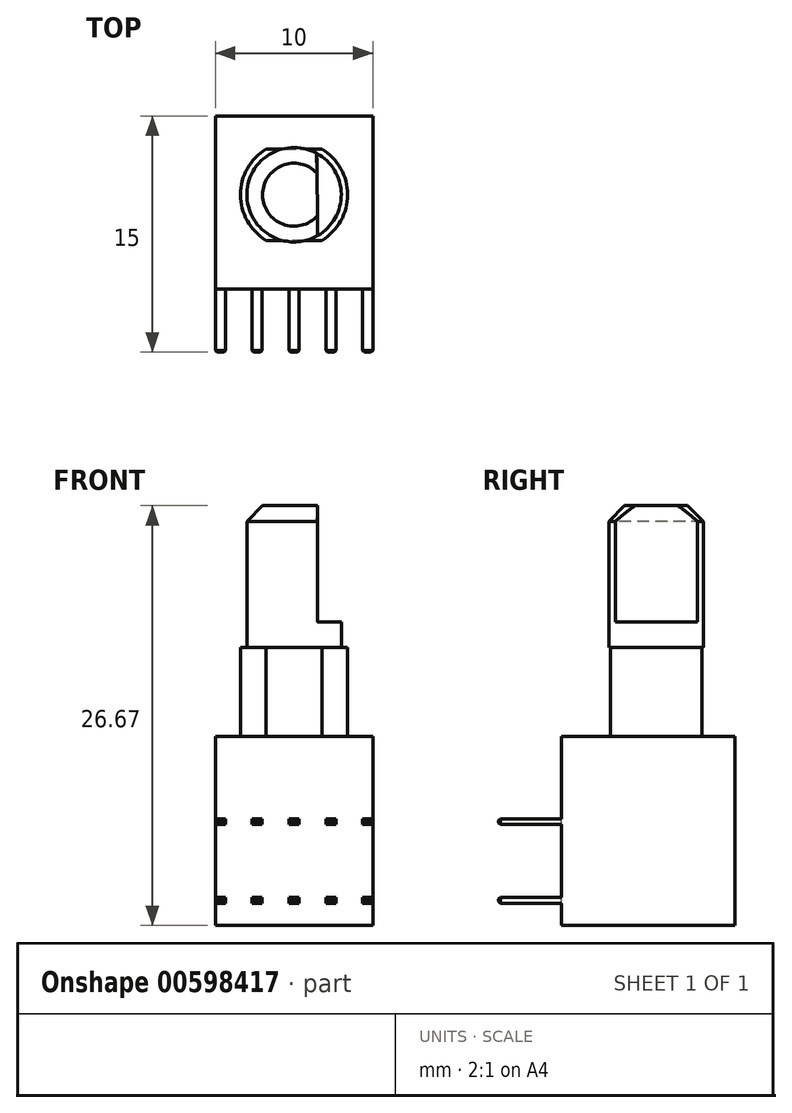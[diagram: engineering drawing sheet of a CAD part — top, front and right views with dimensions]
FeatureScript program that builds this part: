
annotation { "Feature Type Name" : "Feature", "Feature Type Description" : "" }
export const myFeature = defineFeature(function(context is Context, id is Id, definition is map)
    precondition{}
    {
        {
            var Q0;
            Q0=qCreatedBy(makeId("Top.planeOp"),FACE);
            var sketch = newSketch(context, id + "F0", { "sketchPlane" : qUnion([Q0])});
            skLineSegment(sketch, "E0.bottom", {"start": v(5, 5.5) * mm, "end": v(-5, 5.5) * mm});
            skLineSegment(sketch, "E0.top", {"start": v(5, -5.5) * mm, "end": v(-5, -5.5) * mm});
            skLineSegment(sketch, "E0.left", {"start": v(5, 5.5) * mm, "end": v(5, -5.5) * mm});
            skLineSegment(sketch, "E0.right", {"start": v(-5, 5.5) * mm, "end": v(-5, -5.5) * mm});
            skPoint(sketch, "E0.middle", {"position": v(0, 0) * mm});
            skSolve(sketch);
        }
        {
            var Q0;
            Q0=qSketchRegion(id+"F0",true);
            var Q1;
            Q1=makeQuery(id+"F0.imprint","IMPRINT",FACE,{"disambiguationData":[TD([[makeQuery(id+"F0.imprint","IMPRINT",EDGE,{"derivedFrom":sQuery(id+"F0.wireOp",EDGE,"E0.bottom")}),1.0]])]});
            extrude(context, id + "F1", {"entities" : qUnion([Q0, Q1]), "depth" : 12 * mm, "offsetDistance" : 25 * mm});
        }
        {
            var Q0;
            Q0=makeQuery(id+"F1.opExtrude","CAP_FACE",FACE,{"disambiguationData":[OSD([sQuery(id+"F0.wireOp",EDGE,"E0.bottom"),sQuery(id+"F0.wireOp",EDGE,"E0.top"),sQuery(id+"F0.wireOp",EDGE,"E0.left"),sQuery(id+"F0.wireOp",EDGE,"E0.right")])],"isStart":false});
            var sketch = newSketch(context, id + "F2", { "sketchPlane" : qUnion([Q0])});
            skLineSegment(sketch, "E1", {"start": v(-5, 3.4) * mm, "end": v(5, 3.4) * mm, "construction": true});
            skLineSegment(sketch, "E2", {"start": v(-5, -2.4) * mm, "end": v(5, -2.4) * mm, "construction": true});
            skCircle(sketch, "E3", {"center": v(0, 0.5) * mm, "radius": 3.4 * mm});
            skLineSegment(sketch, "E4", {"start": v(-1.77, 3.4) * mm, "end": v(1.77, 3.4) * mm});
            skLineSegment(sketch, "E5", {"start": v(1.77, -2.4) * mm, "end": v(-1.77, -2.4) * mm});
            skSolve(sketch);
        }
        {
            var Q0;
            {var subQ0=sQuery(id+"F2.wireOp",EDGE,"E4");Q0=makeQuery(id+"F2.imprint","IMPRINT",FACE,{"disambiguationData":[TD([[makeQuery(id+"F2.imprint","IMPRINT",EDGE,{"derivedFrom":subQ0}),-1.0]])]});}
            extrude(context, id + "F3", {"entities" : qUnion([Q0]), "operationType" : NewBodyOperationType.ADD, "depth" : 5.67 * mm, "offsetDistance" : 25 * mm});
        }
        {
            var Q0;
            Q0=makeQuery(id+"F3.opExtrude","CAP_FACE",FACE,{"disambiguationData":[OSD([sQuery(id+"F2.wireOp",EDGE,"E3"),sQuery(id+"F2.wireOp",EDGE,"E4"),sQuery(id+"F2.wireOp",EDGE,"E5")])],"isStart":false});
            var sketch = newSketch(context, id + "F4", { "sketchPlane" : qUnion([Q0])});
            skCircle(sketch, "E6", {"center": v(0, 0.5) * mm, "radius": 3 * mm});
            skLineSegment(sketch, "E7", {"start": v(1.44, 3.13) * mm, "end": v(1.5, -2.1) * mm});
            skSolve(sketch);
        }
        {
            var Q0;
            {var subQ0=sQuery(id+"F4.wireOp",EDGE,"E7");Q0=makeQuery(id+"F4.imprint","IMPRINT",FACE,{"disambiguationData":[TD([[makeQuery(id+"F4.imprint","IMPRINT",EDGE,{"derivedFrom":subQ0}),1.0]])]});}
            extrude(context, id + "F5", {"entities" : qUnion([Q0]), "operationType" : NewBodyOperationType.ADD, "depth" : 1.6 * mm, "offsetDistance" : 25 * mm});
        }
        {
            var Q0;
            {var subQ0=sQuery(id+"F4.wireOp",EDGE,"E7");Q0=makeQuery(id+"F4.imprint","IMPRINT",FACE,{"disambiguationData":[TD([[makeQuery(id+"F4.imprint","IMPRINT",EDGE,{"derivedFrom":subQ0}),-1.0]])]});}
            var Q1;
            {var subQ0=sQuery(id+"F4.wireOp",EDGE,"E6");var subQ1=makeQuery(id+"F3.opExtrude","CAP_EDGE",EDGE,{"disambiguationData":[OSD([sQuery(id+"F2.wireOp",EDGE,"E5")])],"isStart":false});var subQ2=makeQuery(id+"F4.imprint","INTERSECT",VERTEX,{"disambiguationData":[OD(0.0)],"derivedFrom":[subQ1,subQ0]});Q1=makeQuery(id+"F4.imprint","IMPRINT",FACE,{"disambiguationData":[TD([[makeQuery(id+"F4.imprint","IMPRINT",EDGE,{"disambiguationData":[TD([[subQ2,-1.0]])],"derivedFrom":subQ0}),1.0]])]});}
            var Q2;
            {var subQ0=sQuery(id+"F4.wireOp",EDGE,"E6");var subQ1=makeQuery(id+"F3.opExtrude","CAP_EDGE",EDGE,{"disambiguationData":[OSD([sQuery(id+"F2.wireOp",EDGE,"E4")])],"isStart":false});var subQ2=makeQuery(id+"F4.imprint","INTERSECT",VERTEX,{"disambiguationData":[OD(0.0)],"derivedFrom":[subQ1,subQ0]});Q2=makeQuery(id+"F4.imprint","IMPRINT",FACE,{"disambiguationData":[TD([[makeQuery(id+"F4.imprint","IMPRINT",EDGE,{"disambiguationData":[TD([[subQ2,-1.0]])],"derivedFrom":subQ0}),1.0]])]});}
            extrude(context, id + "F6", {"entities" : qUnion([Q0, Q1, Q2]), "operationType" : NewBodyOperationType.ADD, "depth" : 9 * mm, "offsetDistance" : 25 * mm});
        }
        {
            var Q0;
            Q0=makeQuery(id+"F6.opExtrude","CAP_EDGE",EDGE,{"disambiguationData":[OSD([sQuery(id+"F4.wireOp",EDGE,"E6")])],"isStart":false});
            chamfer(context, id + "F7", {"entities" : qUnion([Q0]), "width" : 1 * mm, "tangentPropagation" : true});
        }
        {
            var Q0;
            Q0=makeQuery(id+"F1.opExtrude","SWEPT_FACE",FACE,{"disambiguationData":[OSD([sQuery(id+"F0.wireOp",EDGE,"E0.top")])]});
            var sketch = newSketch(context, id + "F8", { "sketchPlane" : qUnion([Q0])});
            skLineSegment(sketch, "E8.bottom", {"start": v(-5, 1.42) * mm, "end": v(-4.36, 1.42) * mm});
            skLineSegment(sketch, "E8.top", {"start": v(-5, 1.78) * mm, "end": v(-4.36, 1.78) * mm});
            skLineSegment(sketch, "E8.left", {"start": v(-5, 1.42) * mm, "end": v(-5, 1.78) * mm});
            skLineSegment(sketch, "E8.right", {"start": v(-4.36, 1.42) * mm, "end": v(-4.36, 1.78) * mm});
            skLineSegment(sketch, "E9.0.1.0", {"start": v(-5, 6.42) * mm, "end": v(-4.36, 6.42) * mm});
            skLineSegment(sketch, "E9.0.1.1", {"start": v(-5, 6.42) * mm, "end": v(-5, 6.78) * mm});
            skLineSegment(sketch, "E9.0.1.2", {"start": v(-4.36, 6.42) * mm, "end": v(-4.36, 6.78) * mm});
            skLineSegment(sketch, "E9.0.1.3", {"start": v(-5, 6.78) * mm, "end": v(-4.36, 6.78) * mm});
            skLineSegment(sketch, "E9.1.0.0", {"start": v(-2.66, 1.42) * mm, "end": v(-2.02, 1.42) * mm});
            skLineSegment(sketch, "E9.1.0.1", {"start": v(-2.66, 1.42) * mm, "end": v(-2.66, 1.78) * mm});
            skLineSegment(sketch, "E9.1.0.2", {"start": v(-2.02, 1.42) * mm, "end": v(-2.02, 1.78) * mm});
            skLineSegment(sketch, "E9.1.0.3", {"start": v(-2.66, 1.78) * mm, "end": v(-2.02, 1.78) * mm});
            skLineSegment(sketch, "E9.1.1.0", {"start": v(-2.66, 6.42) * mm, "end": v(-2.02, 6.42) * mm});
            skLineSegment(sketch, "E9.1.1.1", {"start": v(-2.66, 6.42) * mm, "end": v(-2.66, 6.78) * mm});
            skLineSegment(sketch, "E9.1.1.2", {"start": v(-2.02, 6.42) * mm, "end": v(-2.02, 6.78) * mm});
            skLineSegment(sketch, "E9.1.1.3", {"start": v(-2.66, 6.78) * mm, "end": v(-2.02, 6.78) * mm});
            skLineSegment(sketch, "E9.2.0.0", {"start": v(-0.32, 1.42) * mm, "end": v(0.32, 1.42) * mm});
            skLineSegment(sketch, "E9.2.0.1", {"start": v(-0.32, 1.42) * mm, "end": v(-0.32, 1.78) * mm});
            skLineSegment(sketch, "E9.2.0.2", {"start": v(0.32, 1.42) * mm, "end": v(0.32, 1.78) * mm});
            skLineSegment(sketch, "E9.2.0.3", {"start": v(-0.32, 1.78) * mm, "end": v(0.32, 1.78) * mm});
            skLineSegment(sketch, "E9.2.1.0", {"start": v(-0.32, 6.42) * mm, "end": v(0.32, 6.42) * mm});
            skLineSegment(sketch, "E9.2.1.1", {"start": v(-0.32, 6.42) * mm, "end": v(-0.32, 6.78) * mm});
            skLineSegment(sketch, "E9.2.1.2", {"start": v(0.32, 6.42) * mm, "end": v(0.32, 6.78) * mm});
            skLineSegment(sketch, "E9.2.1.3", {"start": v(-0.32, 6.78) * mm, "end": v(0.32, 6.78) * mm});
            skLineSegment(sketch, "E9.3.0.0", {"start": v(2.02, 1.42) * mm, "end": v(2.66, 1.42) * mm});
            skLineSegment(sketch, "E9.3.0.1", {"start": v(2.02, 1.42) * mm, "end": v(2.02, 1.78) * mm});
            skLineSegment(sketch, "E9.3.0.2", {"start": v(2.66, 1.42) * mm, "end": v(2.66, 1.78) * mm});
            skLineSegment(sketch, "E9.3.0.3", {"start": v(2.02, 1.78) * mm, "end": v(2.66, 1.78) * mm});
            skLineSegment(sketch, "E9.3.1.0", {"start": v(2.02, 6.42) * mm, "end": v(2.66, 6.42) * mm});
            skLineSegment(sketch, "E9.3.1.1", {"start": v(2.02, 6.42) * mm, "end": v(2.02, 6.78) * mm});
            skLineSegment(sketch, "E9.3.1.2", {"start": v(2.66, 6.42) * mm, "end": v(2.66, 6.78) * mm});
            skLineSegment(sketch, "E9.3.1.3", {"start": v(2.02, 6.78) * mm, "end": v(2.66, 6.78) * mm});
            skLineSegment(sketch, "E9.4.0.0", {"start": v(4.36, 1.42) * mm, "end": v(5, 1.42) * mm});
            skLineSegment(sketch, "E9.4.0.1", {"start": v(4.36, 1.42) * mm, "end": v(4.36, 1.78) * mm});
            skLineSegment(sketch, "E9.4.0.2", {"start": v(5, 1.42) * mm, "end": v(5, 1.78) * mm});
            skLineSegment(sketch, "E9.4.0.3", {"start": v(4.36, 1.78) * mm, "end": v(5, 1.78) * mm});
            skLineSegment(sketch, "E9.4.1.0", {"start": v(4.36, 6.42) * mm, "end": v(5, 6.42) * mm});
            skLineSegment(sketch, "E9.4.1.1", {"start": v(4.36, 6.42) * mm, "end": v(4.36, 6.78) * mm});
            skLineSegment(sketch, "E9.4.1.2", {"start": v(5, 6.42) * mm, "end": v(5, 6.78) * mm});
            skLineSegment(sketch, "E9.4.1.3", {"start": v(4.36, 6.78) * mm, "end": v(5, 6.78) * mm});
            skLineSegment(sketch, "E9.direction1", {"start": v(-5, 1.42) * mm, "end": v(-2.66, 1.42) * mm, "construction": true});
            skLineSegment(sketch, "E9.direction2", {"start": v(-5, 1.42) * mm, "end": v(-5, 6.42) * mm, "construction": true});
            skSolve(sketch);
        }
        {
            var Q0;
            Q0=makeQuery(id+"F8.imprint","IMPRINT",FACE,{"disambiguationData":[TD([[makeQuery(id+"F8.imprint","IMPRINT",EDGE,{"derivedFrom":sQuery(id+"F8.wireOp",EDGE,"E9.0.1.0")}),1.0]])]});
            var Q1;
            Q1=makeQuery(id+"F8.imprint","IMPRINT",FACE,{"disambiguationData":[TD([[makeQuery(id+"F8.imprint","IMPRINT",EDGE,{"derivedFrom":sQuery(id+"F8.wireOp",EDGE,"E9.1.1.0")}),1.0]])]});
            var Q2;
            Q2=makeQuery(id+"F8.imprint","IMPRINT",FACE,{"disambiguationData":[TD([[makeQuery(id+"F8.imprint","IMPRINT",EDGE,{"derivedFrom":sQuery(id+"F8.wireOp",EDGE,"E9.2.1.0")}),1.0]])]});
            var Q3;
            Q3=makeQuery(id+"F8.imprint","IMPRINT",FACE,{"disambiguationData":[TD([[makeQuery(id+"F8.imprint","IMPRINT",EDGE,{"derivedFrom":sQuery(id+"F8.wireOp",EDGE,"E9.4.0.0")}),1.0]])]});
            var Q4;
            Q4=makeQuery(id+"F8.imprint","IMPRINT",FACE,{"disambiguationData":[TD([[makeQuery(id+"F8.imprint","IMPRINT",EDGE,{"derivedFrom":sQuery(id+"F8.wireOp",EDGE,"E9.3.0.0")}),1.0]])]});
            var Q5;
            Q5=makeQuery(id+"F8.imprint","IMPRINT",FACE,{"disambiguationData":[TD([[makeQuery(id+"F8.imprint","IMPRINT",EDGE,{"derivedFrom":sQuery(id+"F8.wireOp",EDGE,"E9.2.0.0")}),1.0]])]});
            var Q6;
            Q6=makeQuery(id+"F8.imprint","IMPRINT",FACE,{"disambiguationData":[TD([[makeQuery(id+"F8.imprint","IMPRINT",EDGE,{"derivedFrom":sQuery(id+"F8.wireOp",EDGE,"E9.1.0.0")}),1.0]])]});
            var Q7;
            Q7=makeQuery(id+"F8.imprint","IMPRINT",FACE,{"disambiguationData":[TD([[makeQuery(id+"F8.imprint","IMPRINT",EDGE,{"derivedFrom":sQuery(id+"F8.wireOp",EDGE,"E8.bottom")}),1.0]])]});
            var Q8;
            Q8=makeQuery(id+"F8.imprint","IMPRINT",FACE,{"disambiguationData":[TD([[makeQuery(id+"F8.imprint","IMPRINT",EDGE,{"derivedFrom":sQuery(id+"F8.wireOp",EDGE,"E9.3.1.0")}),1.0]])]});
            var Q9;
            Q9=makeQuery(id+"F8.imprint","IMPRINT",FACE,{"disambiguationData":[TD([[makeQuery(id+"F8.imprint","IMPRINT",EDGE,{"derivedFrom":sQuery(id+"F8.wireOp",EDGE,"E9.4.1.0")}),1.0]])]});
            extrude(context, id + "F9", {"entities" : qUnion([Q0, Q1, Q2, Q3, Q4, Q5, Q6, Q7, Q8, Q9]), "operationType" : NewBodyOperationType.ADD, "depth" : 4 * mm, "offsetDistance" : 25 * mm});
        }
        {
            var Q0;
            Q0=makeQuery(id+"F9.opExtrude","CAP_FACE",FACE,{"disambiguationData":[OSD([sQuery(id+"F8.wireOp",EDGE,"E9.0.1.0"),sQuery(id+"F8.wireOp",EDGE,"E9.0.1.1"),sQuery(id+"F8.wireOp",EDGE,"E9.0.1.2"),sQuery(id+"F8.wireOp",EDGE,"E9.0.1.3")])],"isStart":false});
            var Q1;
            Q1=makeQuery(id+"F9.opExtrude","CAP_FACE",FACE,{"disambiguationData":[OSD([sQuery(id+"F8.wireOp",EDGE,"E9.1.1.0"),sQuery(id+"F8.wireOp",EDGE,"E9.1.1.1"),sQuery(id+"F8.wireOp",EDGE,"E9.1.1.2"),sQuery(id+"F8.wireOp",EDGE,"E9.1.1.3")])],"isStart":false});
            var Q2;
            Q2=makeQuery(id+"F9.opExtrude","CAP_FACE",FACE,{"disambiguationData":[OSD([sQuery(id+"F8.wireOp",EDGE,"E9.2.1.0"),sQuery(id+"F8.wireOp",EDGE,"E9.2.1.1"),sQuery(id+"F8.wireOp",EDGE,"E9.2.1.2"),sQuery(id+"F8.wireOp",EDGE,"E9.2.1.3")])],"isStart":false});
            var Q3;
            Q3=makeQuery(id+"F9.opExtrude","CAP_FACE",FACE,{"disambiguationData":[OSD([sQuery(id+"F8.wireOp",EDGE,"E9.3.1.0"),sQuery(id+"F8.wireOp",EDGE,"E9.3.1.1"),sQuery(id+"F8.wireOp",EDGE,"E9.3.1.2"),sQuery(id+"F8.wireOp",EDGE,"E9.3.1.3")])],"isStart":false});
            var Q4;
            Q4=makeQuery(id+"F9.opExtrude","CAP_FACE",FACE,{"disambiguationData":[OSD([sQuery(id+"F8.wireOp",EDGE,"E9.4.1.0"),sQuery(id+"F8.wireOp",EDGE,"E9.4.1.1"),sQuery(id+"F8.wireOp",EDGE,"E9.4.1.2"),sQuery(id+"F8.wireOp",EDGE,"E9.4.1.3")])],"isStart":false});
            var Q5;
            Q5=makeQuery(id+"F9.opExtrude","CAP_FACE",FACE,{"disambiguationData":[OSD([sQuery(id+"F8.wireOp",EDGE,"E9.4.0.0"),sQuery(id+"F8.wireOp",EDGE,"E9.4.0.1"),sQuery(id+"F8.wireOp",EDGE,"E9.4.0.2"),sQuery(id+"F8.wireOp",EDGE,"E9.4.0.3")])],"isStart":false});
            var Q6;
            Q6=makeQuery(id+"F9.opExtrude","CAP_FACE",FACE,{"disambiguationData":[OSD([sQuery(id+"F8.wireOp",EDGE,"E9.3.0.0"),sQuery(id+"F8.wireOp",EDGE,"E9.3.0.1"),sQuery(id+"F8.wireOp",EDGE,"E9.3.0.2"),sQuery(id+"F8.wireOp",EDGE,"E9.3.0.3")])],"isStart":false});
            var Q7;
            Q7=makeQuery(id+"F9.opExtrude","CAP_FACE",FACE,{"disambiguationData":[OSD([sQuery(id+"F8.wireOp",EDGE,"E9.2.0.0"),sQuery(id+"F8.wireOp",EDGE,"E9.2.0.1"),sQuery(id+"F8.wireOp",EDGE,"E9.2.0.2"),sQuery(id+"F8.wireOp",EDGE,"E9.2.0.3")])],"isStart":false});
            var Q8;
            Q8=makeQuery(id+"F9.opExtrude","CAP_FACE",FACE,{"disambiguationData":[OSD([sQuery(id+"F8.wireOp",EDGE,"E9.1.0.0"),sQuery(id+"F8.wireOp",EDGE,"E9.1.0.1"),sQuery(id+"F8.wireOp",EDGE,"E9.1.0.2"),sQuery(id+"F8.wireOp",EDGE,"E9.1.0.3")])],"isStart":false});
            var Q9;
            Q9=makeQuery(id+"F9.opExtrude","CAP_FACE",FACE,{"disambiguationData":[OSD([sQuery(id+"F8.wireOp",EDGE,"E8.bottom"),sQuery(id+"F8.wireOp",EDGE,"E8.top"),sQuery(id+"F8.wireOp",EDGE,"E8.left"),sQuery(id+"F8.wireOp",EDGE,"E8.right")])],"isStart":false});
            chamfer(context, id + "F10", {"entities" : qUnion([Q0, Q1, Q2, Q3, Q4, Q5, Q6, Q7, Q8, Q9]), "width" : .1 * mm, "tangentPropagation" : true});
        }
    });
